# Revit family: LNC
name_source: partatom
category: Lighting Fixtures
units: mm (PartAtom-declared; Revit-internal decimal feet)

## family parameters
Cut with Voids When Loaded = No
Host = Face
Light Source = No
OmniClass Number = 23.80.70.11
OmniClass Title = Luminaries for Internal Lighting
Part Type = Normal
Room Calculation Point = No
Round Connector Dimension = Use Diameter
Shared = No

## types (5) — shared parameters
Apparent Load = 0 VA
Default Elevation = 48 "
Description = Typical mounting height is up to 12 feet with 40ft fixture spacing (without acrylic diffuser) and 30ft spacing with acrylic diffuser installed.
Glass = White Glass
Lamp = LED Lamp
Manufacturer = EXO
Model = LNC
URL = https://www.currentlighting.com
Voltage = 120 V
Wattage Comments = 12-22 W

## per-type parameters (varying)
| type | Backbox | Photometric Web |
| Bronze | Metal  - Bronze | Web LNC : LNC-7LU-5K-4, 7 LED, 5000K, TYPE 4 |
| Black | Metal - Black | Web LNC : LNC-5LU-3K-2, 5 LED, 3000K, TYPE 2 |
| Grey | Metal - Grey | Web LNC : LNC-5LU-3K-2, 5 LED, 3000K, TYPE 2 |
| Platinum | Metal  - Platinum | Web LNC : LNC-5LU-3K-2, 5 LED, 3000K, TYPE 2 |
| White | Metal  - White | Web LNC : LNC-5LU-3K-2, 5 LED, 3000K, TYPE 2 |

## geometry (parser evidence)
native form markers: Blend x30, Sweep x4
no freeform markers — native parametric forms only
